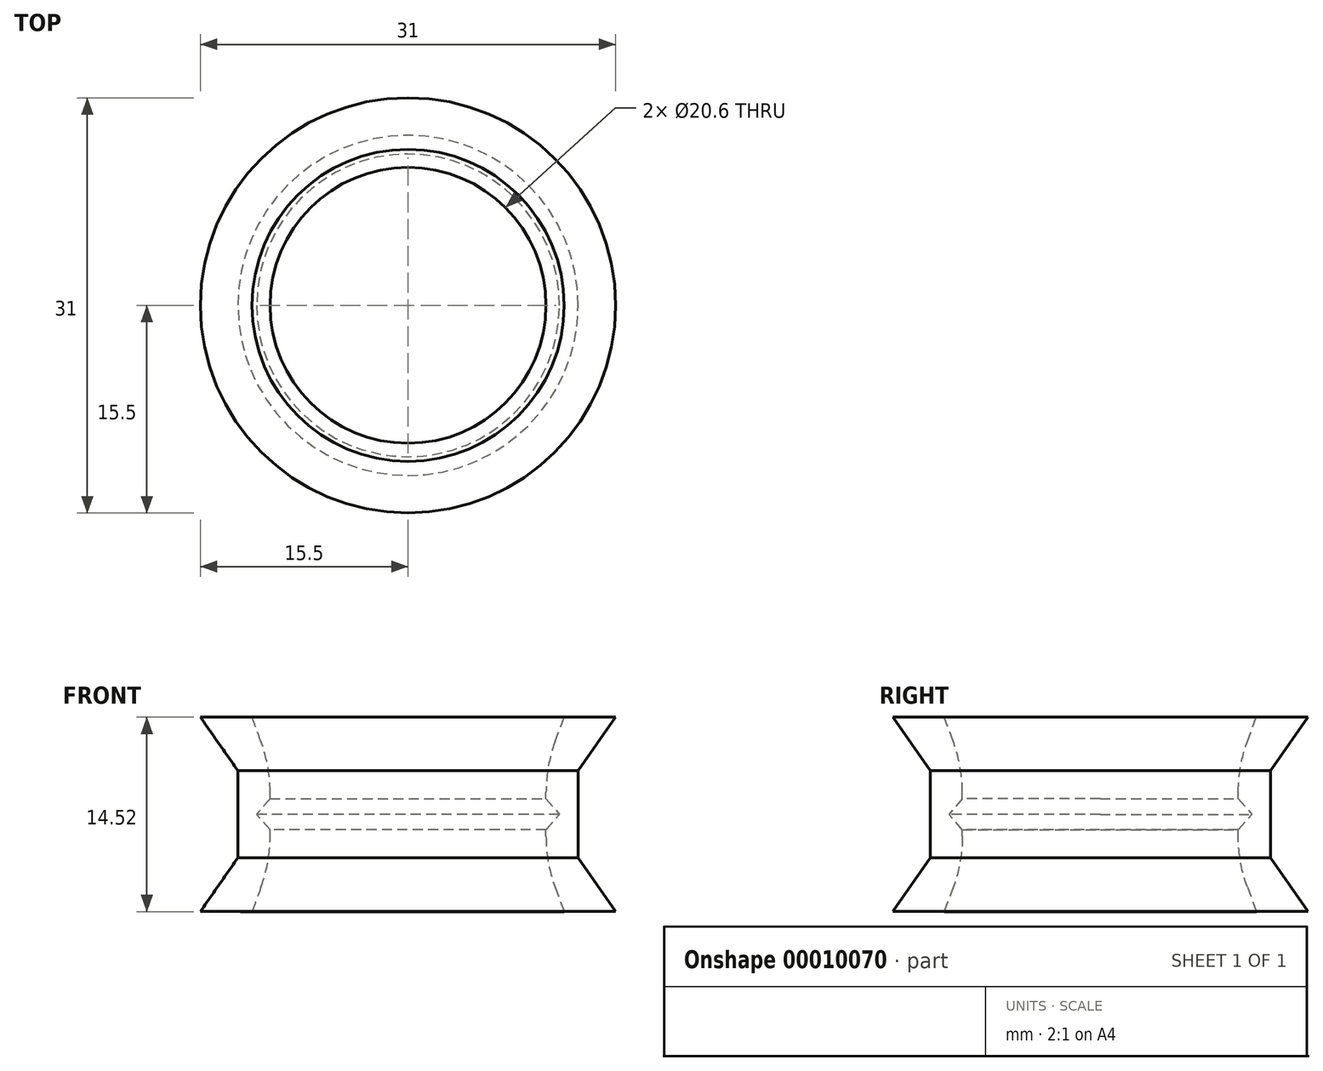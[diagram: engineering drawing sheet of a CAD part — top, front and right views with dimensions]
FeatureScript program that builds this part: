
annotation { "Feature Type Name" : "Feature", "Feature Type Description" : "" }
export const myFeature = defineFeature(function(context is Context, id is Id, definition is map)
    precondition{}
    {
        {
            var Q0;
            Q0=qCreatedBy(makeId("Right.planeOp"),FACE);
            var sketch = newSketch(context, id + "F0", { "sketchPlane" : qUnion([Q0])});
            skLineSegment(sketch, "E0.left", {"start": v(9.8, 2.25) * mm, "end": v(9.8, 1.75) * mm});
            skLineSegment(sketch, "E1", {"start": v(12.7, 3.25) * mm, "end": v(12.7, -3.25) * mm});
            skLineSegment(sketch, "E2", {"start": v(12.7, 3.25) * mm, "end": v(15.5, 7.25) * mm});
            skLineSegment(sketch, "E3", {"start": v(12.7, -3.25) * mm, "end": v(15.5, -7.25) * mm});
            skLineSegment(sketch, "E4", {"start": v(9.8, 1.75) * mm, "end": v(11.3, 0) * mm});
            skLineSegment(sketch, "E5", {"start": v(11.3, 0) * mm, "end": v(9.8, -1.75) * mm});
            skLineSegment(sketch, "E6.trimOffspring", {"start": v(9.8, -1.75) * mm, "end": v(9.8, -2.25) * mm});
            skLineSegment(sketch, "E7", {"start": v(9.8, 2.25) * mm, "end": v(11.65, 7.25) * mm});
            skLineSegment(sketch, "E8", {"start": v(9.8, -2.25) * mm, "end": v(11.65, -7.27) * mm});
            skLineSegment(sketch, "E9", {"start": v(0, -7.25) * mm, "end": v(0, 7.25) * mm, "construction": true});
            skLineSegment(sketch, "E10", {"start": v(11.65, -7.27) * mm, "end": v(15.5, -7.25) * mm});
            skLineSegment(sketch, "E11", {"start": v(11.65, 7.25) * mm, "end": v(15.5, 7.25) * mm});
            skSolve(sketch);
        }
        {
            var Q0;
            Q0=makeQuery(id+"F0.imprint","IMPRINT",FACE,{"disambiguationData":[TD([[makeQuery(id+"F0.imprint","IMPRINT",EDGE,{"derivedFrom":sQuery(id+"F0.wireOp",EDGE,"E0.left")}),1.0]])]});
            var Q1;
            Q1=sQuery(id+"F0.wireOp",EDGE,"E9");
            revolve(context, id + "F1", {"entities" : qUnion([Q0]), "axis" : qUnion([Q1]), "revolveType" : RevolveType.FULL});
        }
        {
            var Q0;
            Q0=makeQuery(id+"F1.opRevolve","SWEPT_FACE",FACE,{"disambiguationData":[OSD([sQuery(id+"F0.wireOp",EDGE,"E11")])]});
            var sketch = newSketch(context, id + "F2", { "sketchPlane" : qUnion([Q0])});
            skCircle(sketch, "E12", {"center": v(0, 0) * mm, "radius": 10.3 * mm});
            skCircle(sketch, "E13", {"center": v(0, 0) * mm, "radius": 9 * mm});
            skSolve(sketch);
        }
        {
            var Q0;
            Q0=makeQuery(id+"F2.imprint","IMPRINT",FACE,{"disambiguationData":[TD([[makeQuery(id+"F2.imprint","IMPRINT",EDGE,{"derivedFrom":sQuery(id+"F2.wireOp",EDGE,"E12")}),1.0]])]});
            extrude(context, id + "F3", {"entities" : qUnion([Q0]), "operationType" : NewBodyOperationType.REMOVE, "oppositeDirection" : true, "depth" : 25 * mm});
        }
        {
            var Q0;
            Q0=makeQuery(id+"F3.boolean.opBoolean","INTERSECT",EDGE,{"derivedFrom":[makeQuery(id+"F1.opRevolve","SWEPT_FACE",FACE,{"disambiguationData":[OSD([sQuery(id+"F0.wireOp",EDGE,"E7")])]}),makeQuery(id+"F3.opExtrude","SWEPT_FACE",FACE,{"disambiguationData":[OSD([sQuery(id+"F2.wireOp",EDGE,"E12")])]})]});
            var Q1;
            Q1=makeQuery(id+"F3.boolean.opBoolean","INTERSECT",EDGE,{"derivedFrom":[makeQuery(id+"F1.opRevolve","SWEPT_FACE",FACE,{"disambiguationData":[OSD([sQuery(id+"F0.wireOp",EDGE,"E8")])]}),makeQuery(id+"F3.opExtrude","SWEPT_FACE",FACE,{"disambiguationData":[OSD([sQuery(id+"F2.wireOp",EDGE,"E12")])]})]});
            fillet(context, id + "F4", {"entities" : qUnion([Q0, Q1]), "radius" : 11 * mm, "tangentPropagation" : true, "allowEdgeOverflow" : false});
        }
    });
